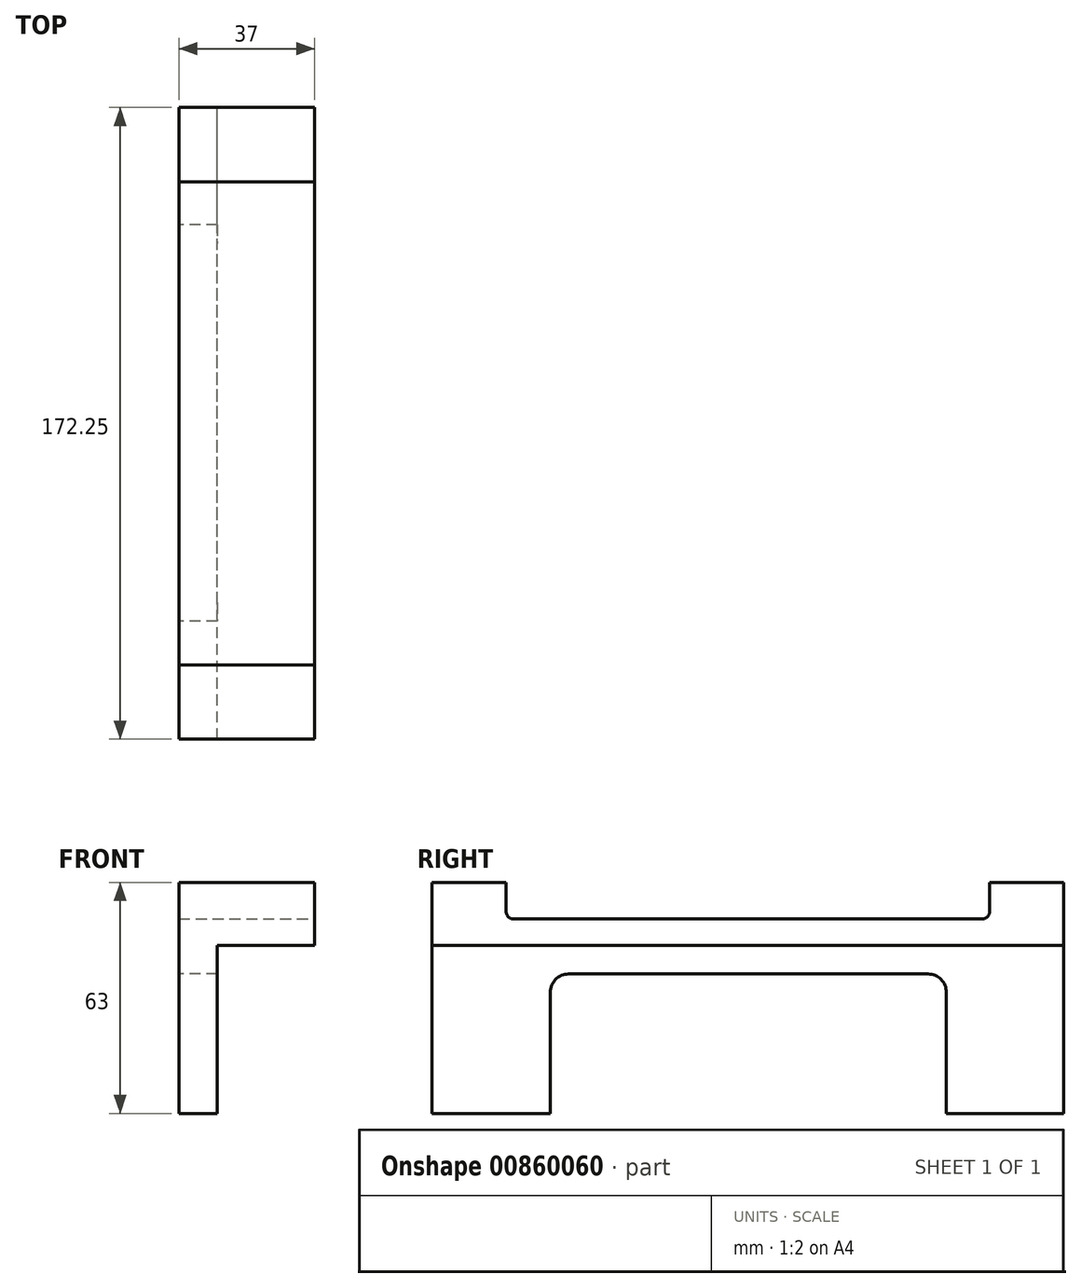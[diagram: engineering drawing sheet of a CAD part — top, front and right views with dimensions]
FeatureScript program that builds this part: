
annotation { "Feature Type Name" : "Feature", "Feature Type Description" : "" }
export const myFeature = defineFeature(function(context is Context, id is Id, definition is map)
    precondition{}
    {
        {
            var Q0;
            Q0=qCreatedBy(makeId("Front.planeOp"),FACE);
            var sketch = newSketch(context, id + "F0", { "sketchPlane" : qUnion([Q0])});
            skLineSegment(sketch, "E0", {"start": v(0, 0) * mm, "end": v(0, 63) * mm});
            skLineSegment(sketch, "E1", {"start": v(0, 63) * mm, "end": v(37, 63) * mm});
            skLineSegment(sketch, "E2", {"start": v(37, 63) * mm, "end": v(37, 45.75) * mm});
            skLineSegment(sketch, "E3", {"start": v(37, 45.75) * mm, "end": v(10.5, 45.75) * mm});
            skLineSegment(sketch, "E4", {"start": v(10.5, 45.75) * mm, "end": v(10.5, 0) * mm});
            skLineSegment(sketch, "E5", {"start": v(10.5, 0) * mm, "end": v(0, 0) * mm});
            skSolve(sketch);
        }
        {
            var Q0;
            Q0 = qSketchRegion(id + "F0", true);
            extrude(context, id + "F1", {"entities" : qUnion([Q0]), "depth" : 172.25 * mm, "offsetDistance" : 25 * mm});
        }
        {
            var Q0;
            Q0=makeQuery(id+"F1.opExtrude","SWEPT_FACE",FACE,{"disambiguationData":[OSD([sQuery(id+"F0.wireOp",EDGE,"E2")])]});
            var sketch = newSketch(context, id + "F2", { "sketchPlane" : qUnion([Q0])});
            skLineSegment(sketch, "E6.bottom", {"start": v(-152, 63) * mm, "end": v(-20.25, 63) * mm});
            skLineSegment(sketch, "E6.top", {"start": v(-150, 53) * mm, "end": v(-22.25, 53) * mm});
            skLineSegment(sketch, "E6.left", {"start": v(-152, 63) * mm, "end": v(-152, 55) * mm});
            skLineSegment(sketch, "E6.right", {"start": v(-20.25, 63) * mm, "end": v(-20.25, 55) * mm});
            skPoint(sketch, "E7.visualSharp", {"position": v(-152, 53) * mm});
            skArc(sketch, "E7.filletArc", {"start": v(-152, 55) * mm, "mid": v(-151.41, 53.59) * mm, "end": v(-150, 53) * mm});
            skPoint(sketch, "E8.visualSharp", {"position": v(-20.25, 53) * mm});
            skArc(sketch, "E8.filletArc", {"start": v(-22.25, 53) * mm, "mid": v(-20.84, 53.59) * mm, "end": v(-20.25, 55) * mm});
            skSolve(sketch);
        }
        {
            var Q0;
            Q0 = qSketchRegion(id + "F2", true);
            extrude(context, id + "F3", {"entities" : qUnion([Q0]), "operationType" : NewBodyOperationType.REMOVE, "oppositeDirection" : true, "depth" : 50 * mm, "offsetDistance" : 25 * mm});
        }
        {
            var Q0;
            Q0=makeQuery(id+"F1.opExtrude","SWEPT_FACE",FACE,{"disambiguationData":[OSD([sQuery(id+"F0.wireOp",EDGE,"E0")])]});
            var sketch = newSketch(context, id + "F4", { "sketchPlane" : qUnion([Q0])});
            skLineSegment(sketch, "E9.bottom", {"start": v(32, 0) * mm, "end": v(140, 0) * mm});
            skLineSegment(sketch, "E9.top", {"start": v(37, 38) * mm, "end": v(135, 38) * mm});
            skLineSegment(sketch, "E9.left", {"start": v(32, 0) * mm, "end": v(32, 33) * mm});
            skLineSegment(sketch, "E9.right", {"start": v(140, 0) * mm, "end": v(140, 33) * mm});
            skPoint(sketch, "E10.visualSharp", {"position": v(32, 38) * mm});
            skArc(sketch, "E10.filletArc", {"start": v(37, 38) * mm, "mid": v(33.46, 36.54) * mm, "end": v(32, 33) * mm});
            skPoint(sketch, "E11.visualSharp", {"position": v(140, 38) * mm});
            skArc(sketch, "E11.filletArc", {"start": v(140, 33) * mm, "mid": v(138.54, 36.54) * mm, "end": v(135, 38) * mm});
            skSolve(sketch);
        }
        {
            var Q0;
            Q0 = qSketchRegion(id + "F4", true);
            extrude(context, id + "F5", {"entities" : qUnion([Q0]), "operationType" : NewBodyOperationType.REMOVE, "oppositeDirection" : true, "depth" : 25 * mm, "offsetDistance" : 25 * mm});
        }
    });
